# Revit family: FU_Stool_Sandler_Celina 4-14
name_source: partatom
category: Furniture
units: mm (PartAtom-declared; Revit-internal decimal feet)

## family parameters
Always vertical = Yes
Cut with Voids When Loaded = No
OmniClass Number = 23.40.20.00
OmniClass Title = General Furniture and Specialties
Room Calculation Point = No
Shared = No
Work Plane-Based = No

## types (1)
- Celina 4.14
    Default Elevation = 0 mm  [stored 0 ft]
    Depth = 550 mm
    Description = Counterstool with a wooden seat and upholstered back panel. The frame is in solid beech.
    Frame = Wood - Beech - Walnut - V
    Height = 1090 mm  [stored 3.57612 ft]
    Manufacturer = Sandler
    Model = Celina 4.14
    URL = https://www.sandlerseating.com
    Upholstery = Fabric - Mainline Flax - Pimlico MLF34
    Width = 475 mm  [stored 1.5584 ft]

note: [stored X ft] marks values corroborated as IEEE doubles in the binary element streams (Revit-internal decimal feet)

## geometry (parser evidence)
native form markers: Sweep x5
no freeform markers — native parametric forms only
